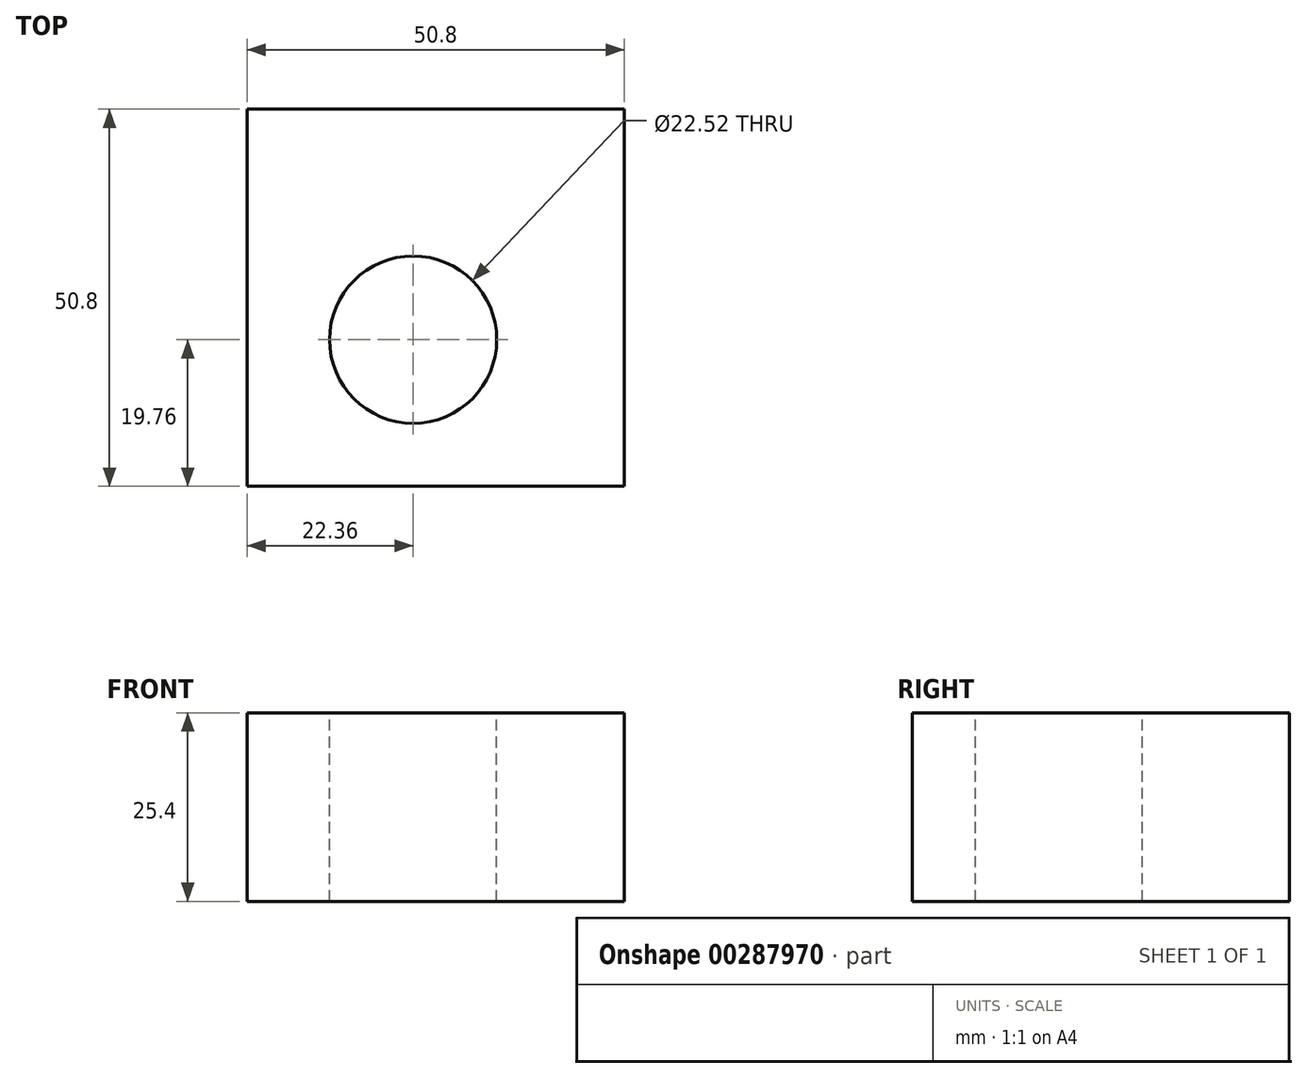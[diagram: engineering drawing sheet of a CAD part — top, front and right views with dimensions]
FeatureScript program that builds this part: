
annotation { "Feature Type Name" : "Feature", "Feature Type Description" : "" }
export const myFeature = defineFeature(function(context is Context, id is Id, definition is map)
    precondition{}
    {
        {
            var Q0;
            Q0=qCreatedBy(makeId("Top.planeOp"),FACE);
            var sketch = newSketch(context, id + "F0", { "sketchPlane" : qUnion([Q0])});
            skLineSegment(sketch, "E0.bottom", {"start": v(-22.36, 31.04) * mm, "end": v(28.44, 31.04) * mm});
            skLineSegment(sketch, "E0.top", {"start": v(-22.36, -19.76) * mm, "end": v(28.44, -19.76) * mm});
            skLineSegment(sketch, "E0.left", {"start": v(-22.36, 31.04) * mm, "end": v(-22.36, -19.76) * mm});
            skLineSegment(sketch, "E0.right", {"start": v(28.44, 31.04) * mm, "end": v(28.44, -19.76) * mm});
            skCircle(sketch, "E1", {"center": v(0, 0) * mm, "radius": 11.26 * mm});
            skSolve(sketch);
        }
        {
            var Q0;
            Q0 = qSketchRegion(id + "F0", true);
            extrude(context, id + "F1", {"entities" : qUnion([Q0]), "oppositeDirection" : true, "depth" : 25.4 * mm});
        }
    });
